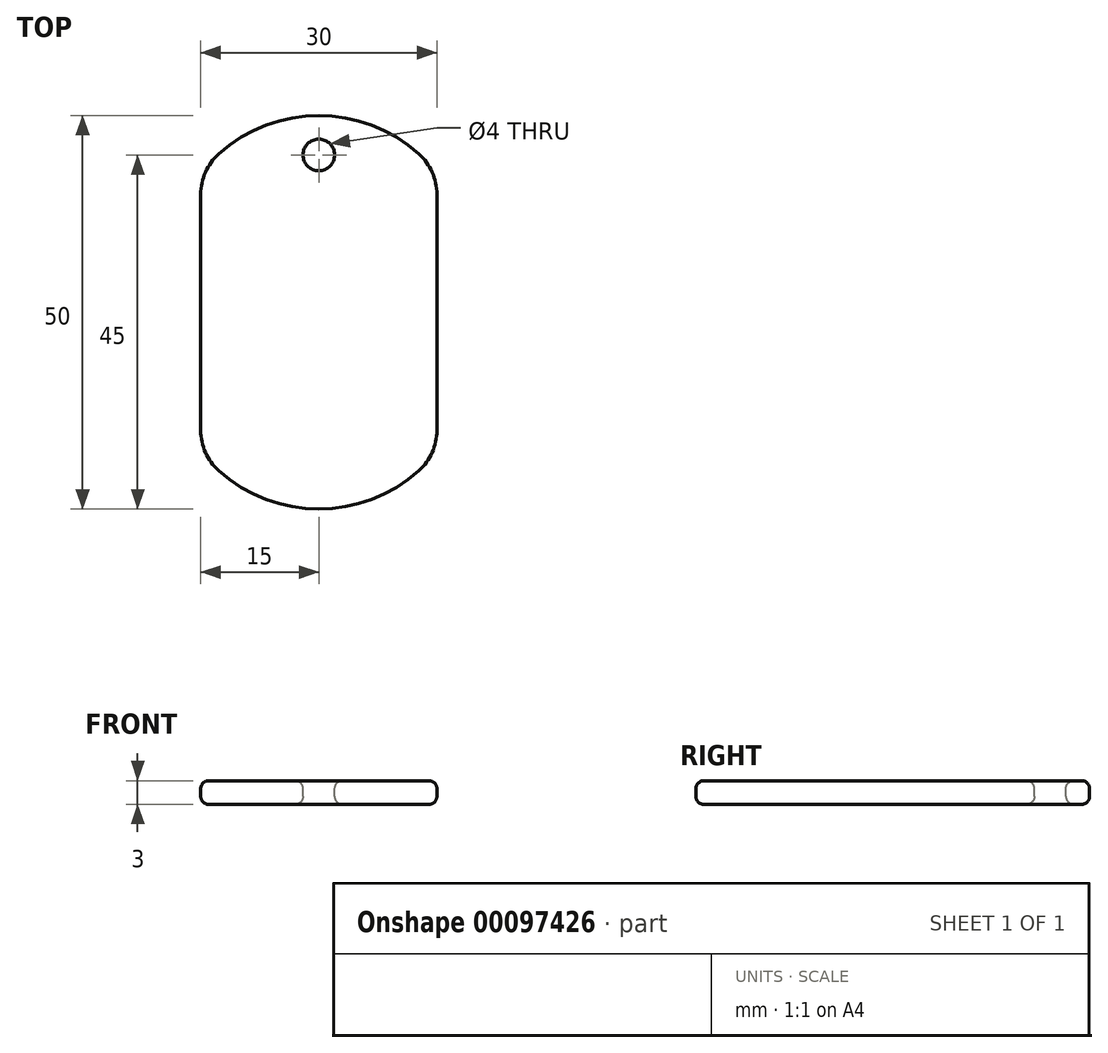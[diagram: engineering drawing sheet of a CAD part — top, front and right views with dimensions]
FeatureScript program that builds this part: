
annotation { "Feature Type Name" : "Feature", "Feature Type Description" : "" }
export const myFeature = defineFeature(function(context is Context, id is Id, definition is map)
    precondition{}
    {
        {
            var Q0;
            Q0=qCreatedBy(makeId("Top.planeOp"),FACE);
            var sketch = newSketch(context, id + "F0", { "sketchPlane" : qUnion([Q0])});
            skLineSegment(sketch, "E0", {"start": v(0, 0) * mm, "end": v(25.46, 0) * mm, "construction": true});
            skLineSegment(sketch, "E1.left", {"start": v(15, 15) * mm, "end": v(15, -15) * mm});
            skLineSegment(sketch, "E1.right", {"start": v(-15, 15) * mm, "end": v(-15, -15) * mm});
            skPoint(sketch, "E1.middle", {"position": v(0, 0) * mm});
            skArc(sketch, "E2", {"start": v(-12.73, 20.1) * mm, "mid": v(0, 25) * mm, "end": v(12.73, 20.1) * mm});
            skArc(sketch, "E3", {"start": v(-15, 15) * mm, "mid": v(-14.4, 17.8) * mm, "end": v(-12.73, 20.1) * mm});
            skArc(sketch, "E4", {"start": v(15, 15) * mm, "mid": v(14.4, 17.8) * mm, "end": v(12.73, 20.1) * mm});
            skPoint(sketch, "E5", {"position": v(0, 25) * mm});
            skArc(sketch, "E6.MirrorCS", {"start": v(-15, -15) * mm, "mid": v(-14.4, -17.8) * mm, "end": v(-12.73, -20.1) * mm});
            skArc(sketch, "E7.MirrorCS", {"start": v(-12.73, -20.1) * mm, "mid": v(0, -25) * mm, "end": v(12.73, -20.1) * mm});
            skArc(sketch, "E8.MirrorCS", {"start": v(15, -15) * mm, "mid": v(14.4, -17.8) * mm, "end": v(12.73, -20.1) * mm});
            skSolve(sketch);
        }
        {
            var Q0;
            Q0 = qSketchRegion(id + "F0", true);
            extrude(context, id + "F1", {"entities" : qUnion([Q0]), "depth" : 3 * mm});
        }
        {
            var Q0;
            Q0=makeQuery(id+"F1.opExtrude","CAP_FACE",FACE,{"disambiguationData":[OSD([sQuery(id+"F0.wireOp",EDGE,"E1.left"),sQuery(id+"F0.wireOp",EDGE,"E1.right"),sQuery(id+"F0.wireOp",EDGE,"E2"),sQuery(id+"F0.wireOp",EDGE,"E3"),sQuery(id+"F0.wireOp",EDGE,"E4"),sQuery(id+"F0.wireOp",EDGE,"E6.MirrorCS"),sQuery(id+"F0.wireOp",EDGE,"E7.MirrorCS"),sQuery(id+"F0.wireOp",EDGE,"E8.MirrorCS")])],"isStart":false});
            var sketch = newSketch(context, id + "F2", { "sketchPlane" : qUnion([Q0])});
            skPoint(sketch, "E9", {"position": v(0, 20) * mm});
            skSolve(sketch);
        }
        {
            var Q0;
            Q0=sQuery(id+"F2.wireOp",VERTEX,"E9");
            var Q1;
            Q1=makeQuery(id+"F1.opExtrude","SWEPT_BODY",BODY,{"disambiguationData":[OSD([sQuery(id+"F0.wireOp",EDGE,"E1.left"),sQuery(id+"F0.wireOp",EDGE,"E1.right"),sQuery(id+"F0.wireOp",EDGE,"E2"),sQuery(id+"F0.wireOp",EDGE,"E3"),sQuery(id+"F0.wireOp",EDGE,"E4"),sQuery(id+"F0.wireOp",EDGE,"E6.MirrorCS"),sQuery(id+"F0.wireOp",EDGE,"E7.MirrorCS"),sQuery(id+"F0.wireOp",EDGE,"E8.MirrorCS")])]});
            hole(context, id + "F3", {"style" : HoleStyle.SIMPLE, "endStyle" : HoleEndStyle.THROUGH, "holeDiameter" : 4 * mm, "locations" : qUnion([Q0]), "scope" : qUnion([Q1]), "isTappedThrough" : true});
        }
        {
            var Q0;
            Q0=makeQuery(id+"F1.opExtrude","CAP_FACE",FACE,{"disambiguationData":[OSD([sQuery(id+"F0.wireOp",EDGE,"E1.left"),sQuery(id+"F0.wireOp",EDGE,"E1.right"),sQuery(id+"F0.wireOp",EDGE,"E2"),sQuery(id+"F0.wireOp",EDGE,"E3"),sQuery(id+"F0.wireOp",EDGE,"E4"),sQuery(id+"F0.wireOp",EDGE,"E6.MirrorCS"),sQuery(id+"F0.wireOp",EDGE,"E7.MirrorCS"),sQuery(id+"F0.wireOp",EDGE,"E8.MirrorCS")])],"isStart":false});
            var Q1;
            Q1=makeQuery(id+"F1.opExtrude","CAP_FACE",FACE,{"disambiguationData":[OSD([sQuery(id+"F0.wireOp",EDGE,"E1.left"),sQuery(id+"F0.wireOp",EDGE,"E1.right"),sQuery(id+"F0.wireOp",EDGE,"E2"),sQuery(id+"F0.wireOp",EDGE,"E3"),sQuery(id+"F0.wireOp",EDGE,"E4"),sQuery(id+"F0.wireOp",EDGE,"E6.MirrorCS"),sQuery(id+"F0.wireOp",EDGE,"E7.MirrorCS"),sQuery(id+"F0.wireOp",EDGE,"E8.MirrorCS")])],"isStart":true});
            fillet(context, id + "F4", {"entities" : qUnion([Q0, Q1]), "radius" : 1 * mm, "tangentPropagation" : true, "allowEdgeOverflow" : false});
        }
    });
